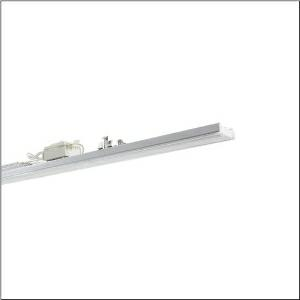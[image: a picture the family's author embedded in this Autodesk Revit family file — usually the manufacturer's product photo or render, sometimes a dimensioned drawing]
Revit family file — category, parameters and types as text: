
# Revit family: licross_r__11_recessed_ho_51tl12dnec5m_e080
name_source: partatom
category: Lighting Fixtures
units: mm (PartAtom-declared; Revit-internal decimal feet)

## family parameters
Cut with Voids When Loaded = No
Host = Face
Light Source = No
Part Type = Normal
Room Calculation Point = No
Round Connector Dimension = Use Diameter
Shared = No

## types (1)
- --- (1 x LED, 12970 lm, 77 W, 5000K)
    Apparent Load = 77 VA
    CIE Flux Codes = 66 91 98 100 100
    Color Rendering = 90
    Color Temperature = 5000K
    Default Elevation = 1800 mm
    Description = Licross® 11 Recessed HO, luminaire insert, of sheet steel, coil coated, white, length: 1.500mm, width: 66mm, height: 67mm, LED rated luminous flux: 12.970lm, light colour: 950, control gear: DALI 2, with plug, 5-pole, with phase selection, mains connection: 220..240V, AC, 50/60Hz, rated input power: 77W, internal wiring halogen-free, primary optical cover: cover, of PMMA, light emission: direct distribution, primary light characteristic: symmetric, protection rating (complete): IP40, insulation class (complete): insulation class I (protective earthing), certification: CE, ENEC, VDE, UKCA, protection symbol: D if used in an environment without relevant dust loads with corresponding accessories, impact resistance: IK06, permissible ambient temperature for indoor applications: -25..+30°C, corresponds to IFS (International Featured Standards) requirements for safety and quality in the food industry, reducing of maximum allowable ambient temperature of 5°C with ceiling mounting, LABS conformity tested according to VDMA 24364:2018-05, packaging unit: 1 piece
    Height = 58 mm
    Lamp = 1 x LED
    Lamp Light Flux = 12970 lm
    Lamp Power = 77 W
    Lamp count = 1
    Length = 1500 mm
    Luminous efficacy = 168 lm/W
    Manufacturer = Siteco
    ModVariant = No
    Model = 51TL12DNEC5M
    Mounting Place = Ceiling
    Mounting Type = Pendant
    Number of Poles = 1
    OnlyDefault = Yes
    Power Factor = 1
    Product Name = Licross® 11 Recessed HO
    Product group = luminaire insert | ceiling pendant
    ProductGroupID = 902
    Protection Class = Protection class I
    Protection Degree = IP 40
    RLX_Detail_Level = 1
    RLX_Emergency_Light_Flux = 0 lm
    RLX_Emergency_Type = 0
    RLX_Emergency_Type_DB = No
    RlxData = <blob elided: 24557 chars, md5=59b137f3>
    Socket = socket
    Standby Power = 0 W
    System Light Flux = 12970 lm
    System Power = 77 W
    Type Comments = factory setting: luminous flux: 100 % | dim-lin: 254 | 522 mA
    Type Image = l_1296930.jpg
    URL = http://relux.com
    VarID = @adj_069537
    Voltage = 0 V
    Weight = 0.00 kg
    Width = 66 mm

## geometry (parser evidence)
native form markers: Blend x4, Sweep x10
no freeform markers — native parametric forms only
